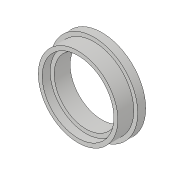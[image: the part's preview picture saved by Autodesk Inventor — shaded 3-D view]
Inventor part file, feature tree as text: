
AUTODESK INVENTOR PART (.ipt)
format: ipt  version: 2018.3 (Build 223284000, 284)  size: 114,176 bytes
history: native  units: in
note: dims shown in document units (in); Inventor stores cm internally (conversion verified against a paired STEP export)
features: extrude x4, sketch x4
ambient origin geometry x8: Origin, YZ Plane, XZ Plane, XY Plane, X Axis, Y Axis, Z Axis, Center Point
bodies: Solid1 (feature_tree)
feature tree (8):
  extrude  "Extrusion1"  Depth=0.6875in
  extrude  "Extrusion2"  Depth=0.0625in TaperAngle=0.0deg
  extrude  "Extrusion3"  Depth=0.125in TaperAngle=0.0deg
  extrude  "Extrusion4"  Depth=0.0625in TaperAngle=0.0deg
  sketch  "Sketch1"  dims[d0=0.5in d3=0.6875in]
  sketch  "Sketch2"  dims[d4=0.0312in d5=0.0625in d6=0.0in]
  sketch  "Sketch3"  dims[d7=0.5in d8=0.6875in d9=0.0312in d10=0.0625in d11=0.0in d12=0.125in d13=0.0in]
  sketch  "Sketch4"  dims[d14=0.0312in d15=0.0625in d16=0.0in]
